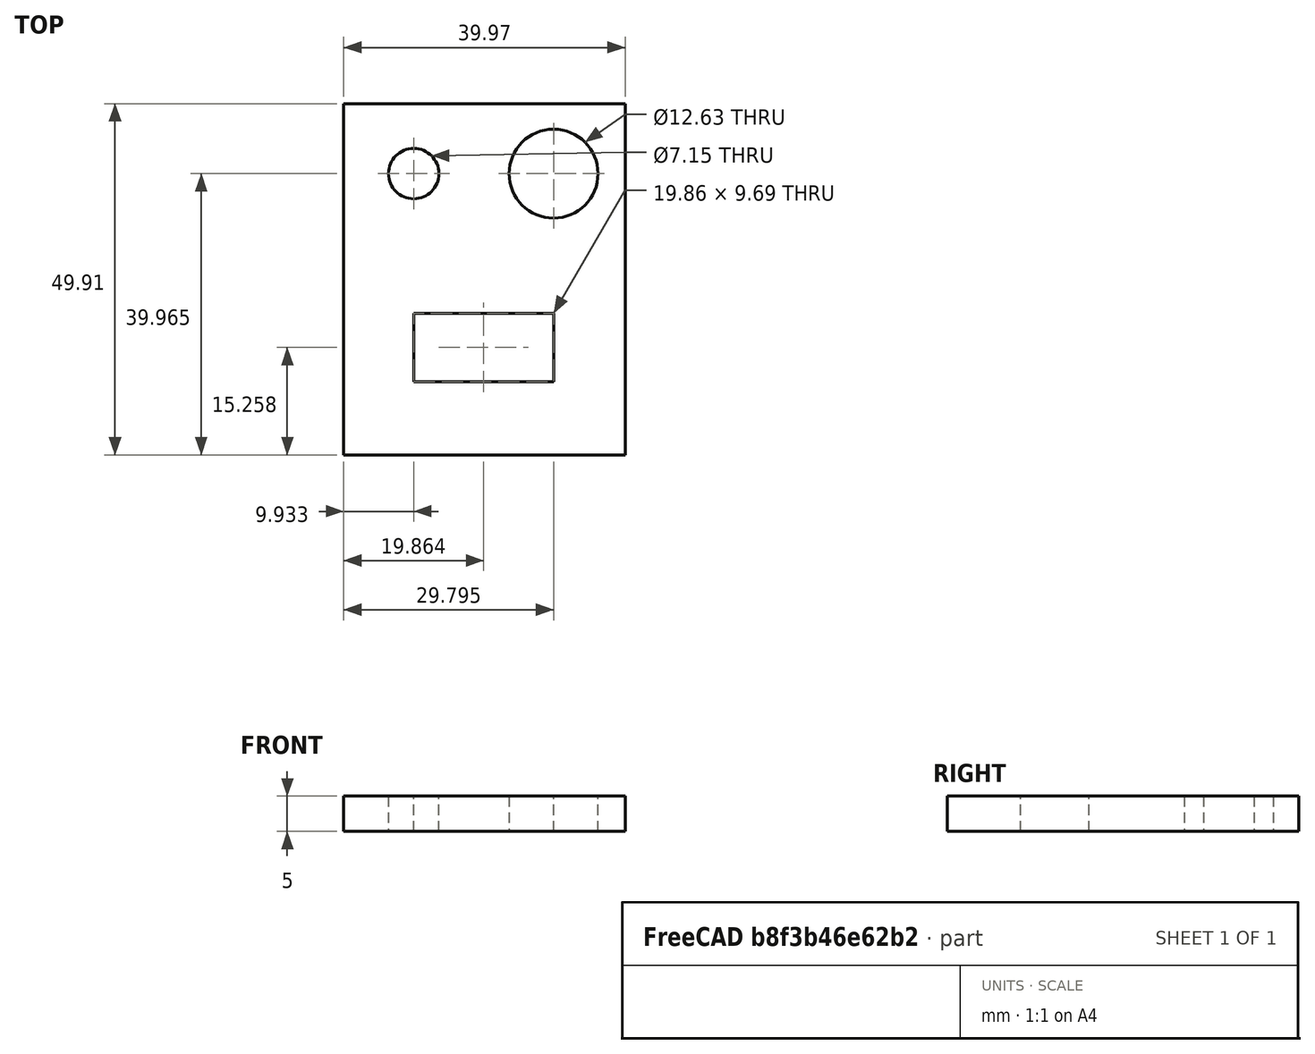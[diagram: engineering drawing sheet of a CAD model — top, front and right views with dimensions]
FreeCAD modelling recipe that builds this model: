
FCSTD DOCUMENT  (FreeCAD 0.21R33694 (Git))
Label: Solución Reto 2
License: All rights reserved
LicenseURL: http://en.wikipedia.org/wiki/All_rights_reserved
objects: Sketcher::SketchObject×1, PartDesign::Pad×1, PartDesign::Body×1
note: 4 computed .brp shape members not serialized (recipe doc carries the construction recipe); baked Part::Feature solids carry a one-line shape summary decoded from their .brp

FEATURE [Sketcher::SketchObject] Sketch
  FullyConstrained = false
  MapMode = 5
  Support = -> [XY_Plane]
  sketch-geometry (10):
    g0: LineSegment StartX=-19.971 StartY=19.7413 StartZ=0 EndX=19.999 EndY=19.7413 EndZ=0
    g1: LineSegment StartX=19.999 StartY=19.7413 StartZ=0 EndX=19.999 EndY=-30.1727 EndZ=0
    g2: LineSegment StartX=19.999 StartY=-30.1727 StartZ=0 EndX=-19.971 EndY=-30.1727 EndZ=0
    g3: LineSegment StartX=-19.971 StartY=-30.1727 StartZ=0 EndX=-19.971 EndY=19.7413 EndZ=0
    g4: Circle CenterX=-10.0373 CenterY=9.79488 CenterZ=0 NormalX=0 NormalY=0 NormalZ=1 AngleXU=0 Radius=3.57646
    g5: Circle CenterX=9.82538 CenterY=9.79488 CenterZ=0 NormalX=0 NormalY=0 NormalZ=1 AngleXU=0 Radius=6.31654
    g6: LineSegment StartX=-10.0373 StartY=-10.0678 StartZ=0 EndX=9.82538 EndY=-10.0678 EndZ=0
    g7: LineSegment StartX=9.82538 StartY=-10.0678 StartZ=0 EndX=9.82538 EndY=-19.7569 EndZ=0
    g8: LineSegment StartX=9.82538 StartY=-19.7569 StartZ=0 EndX=-10.0373 EndY=-19.7569 EndZ=0
    g9: LineSegment StartX=-10.0373 StartY=-19.7569 StartZ=0 EndX=-10.0373 EndY=-10.0678 EndZ=0
  constraints (16):
    c: Coincident(g0,g1)
    c: Coincident(g1,g2)
    c: Coincident(g2,g3)
    c: Coincident(g3,g0)
    c: Horizontal(g0)
    c: Horizontal(g2)
    c: Vertical(g1)
    c: Vertical(g3)
    c: Coincident(g6,g7)
    c: Coincident(g7,g8)
    c: Coincident(g8,g9)
    c: Coincident(g9,g6)
    c: Horizontal(g6)
    c: Horizontal(g8)
    c: Vertical(g7)
    c: Vertical(g9)
FEATURE [PartDesign::Pad] Pad
  Direction = (0,0,1)
  Length = 5
  Length2 = 10
  Profile = -> Sketch
  ReferenceAxis = -> Sketch [N_Axis]
  Refine = true
  Type = 0
FEATURE [PartDesign::Body] Body  label="Cuerpo"
  Group = -> [Sketch,Pad]
  Origin = -> Origin
  Tip = -> Pad
